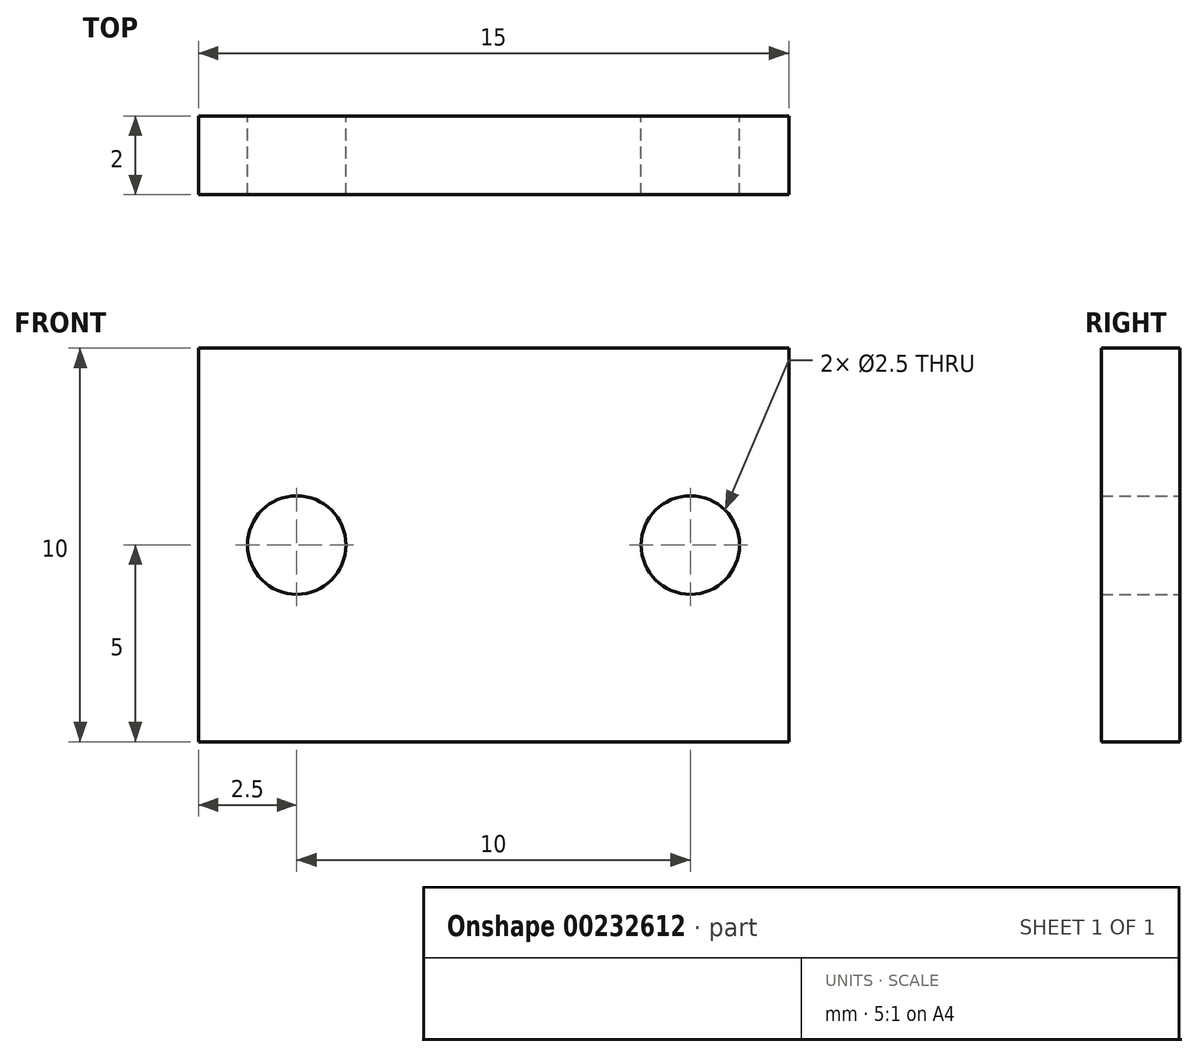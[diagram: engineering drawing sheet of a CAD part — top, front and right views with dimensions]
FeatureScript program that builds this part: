
annotation { "Feature Type Name" : "Feature", "Feature Type Description" : "" }
export const myFeature = defineFeature(function(context is Context, id is Id, definition is map)
    precondition{}
    {
        {
            var Q0;
            Q0=qCreatedBy(makeId("Front.planeOp"),FACE);
            var sketch = newSketch(context, id + "F0", { "sketchPlane" : qUnion([Q0])});
            skLineSegment(sketch, "E0.bottom", {"start": v(0, 0) * mm, "end": v(15, 0) * mm});
            skLineSegment(sketch, "E0.top", {"start": v(0, 10) * mm, "end": v(15, 10) * mm});
            skLineSegment(sketch, "E0.left", {"start": v(0, 0) * mm, "end": v(0, 10) * mm});
            skLineSegment(sketch, "E0.right", {"start": v(15, 0) * mm, "end": v(15, 10) * mm});
            skCircle(sketch, "E1", {"center": v(2.5, 5) * mm, "radius": 1.25 * mm});
            skCircle(sketch, "E2", {"center": v(12.5, 5) * mm, "radius": 1.25 * mm});
            skSolve(sketch);
        }
        {
            var Q0;
            Q0=qSketchRegion(id+"F0",true);
            extrude(context, id + "F1", {"entities" : qUnion([Q0]), "depth" : 2 * mm});
        }
    });
